# Revit family: 66666
name_source: partatom
category: Lighting Fixtures
units: mm (PartAtom-declared; Revit-internal decimal feet)

## family parameters
Cut with Voids When Loaded = No
Host = Face
Light Source = Yes
OmniClass Number = 23.80.70.11
OmniClass Title = Luminaries for Internal Lighting
Part Type = Normal
Room Calculation Point = No
Round Connector Dimension = Use Diameter
Shared = No

## types (1)
- Not a Type - Load Type Catalog!
    Apparent Load = 0 VA
    Assembly Code = D5020200
    CRI = 80
    Color Filter = 16777215
    Default Elevation = 4' - 0"
    Description = Optimo Direct-Indirect
    Dimming Lamp Color Temperature Shift = <None>
    Direct Distribution = SD
    Edition number = 1
    Electrical Disconnect = Yes
    Emit Shape Visible in Rendering = No
    Emit from Rectangle Length = 3' - 11 1/2"
    Emit from Rectangle Width = 0' - 3"
    Frequency = 0 Hz
    Height = 0' - 3"
    Indirect Distribution = CL
    Input Wattage = 0 W
    Keynote = 16500
    Lamp = LED
    Lamp length 4' = Yes
    Lamp length 8' = No
    Length = 4' - 0"
    Manufacturer = StarTek Lighting
    Number of Poles = 1
    Phase = 1
    Photometric Note = Import IES files https://starteklightingamerica.com
    Photometric Web File = Generic Light Source Shown : Please download and link the IES file that best matches your fixture specification
    Power Factor = 1
    Product Guid = 238ea46f-5e4f-4156-8c1f-09dc676d21ec
    Product data url = https://www.bimobject.com
    Tilt Angle = 90.00°
    Type Comments = Linear Lighting Fixture
    URL = https://starteklightingamerica.com
    Voltage = 120 V
    Weight = 0.00 lbf
    Width = 0' - 3"
    z_AC05 = Aircraft Cable : with Canopy 5' (AC05)
    z_AC10 = Aircraft Cable : with Canopy 10' (AC10)
    z_RO End = Run : End Fixture
    z_RO Middle = Run : Middle Fixture
    z_RO Standalone = Run : Standalone Fixture
    z_RO Start = Run : Start Fixture
    z_RS12 = Stem Mount with Canopy (SMC) : 12"
    z_RS15 = Stem Mount with Canopy (SMC) : 15"
    z_RS18 = Stem Mount with Canopy (SMC) : 18"
    z_RS21 = Stem Mount with Canopy (SMC) : 21"
    z_RS24 = Stem Mount with Canopy (SMC) : 24"
    z_RS27 = Stem Mount with Canopy (SMC) : 27"
    z_RS30 = Stem Mount with Canopy (SMC) : 30"
    z_RS36 = Stem Mount with Canopy (SMC) : 36"
    z_RS42 = Stem Mount with Canopy (SMC) : 42"
    z_RS48 = Stem Mount with Canopy (SMC) : 48"
    z_RS54 = Stem Mount with Canopy (SMC) : 54"
    z_RS6 = Stem Mount with Canopy (SMC) : 6"
    z_RS60 = Stem Mount with Canopy (SMC) : 60"
    z_RS66 = Stem Mount with Canopy (SMC) : 66"
    z_RS72 = Stem Mount with Canopy (SMC) : 72"
    z_RS78 = Stem Mount with Canopy (SMC) : 78"
    z_RS8 = Stem Mount with Canopy (SMC) : 8"
    z_RS84 = Stem Mount with Canopy (SMC) : 84"
    z_RS9 = Stem Mount with Canopy (SMC) : 9"
    z_RS90 = Stem Mount with Canopy (SMC) : 90"
    z_RS96 = Stem Mount with Canopy (SMC) : 96"

## geometry (parser evidence)
native form markers: Sweep x10
no freeform markers — native parametric forms only
